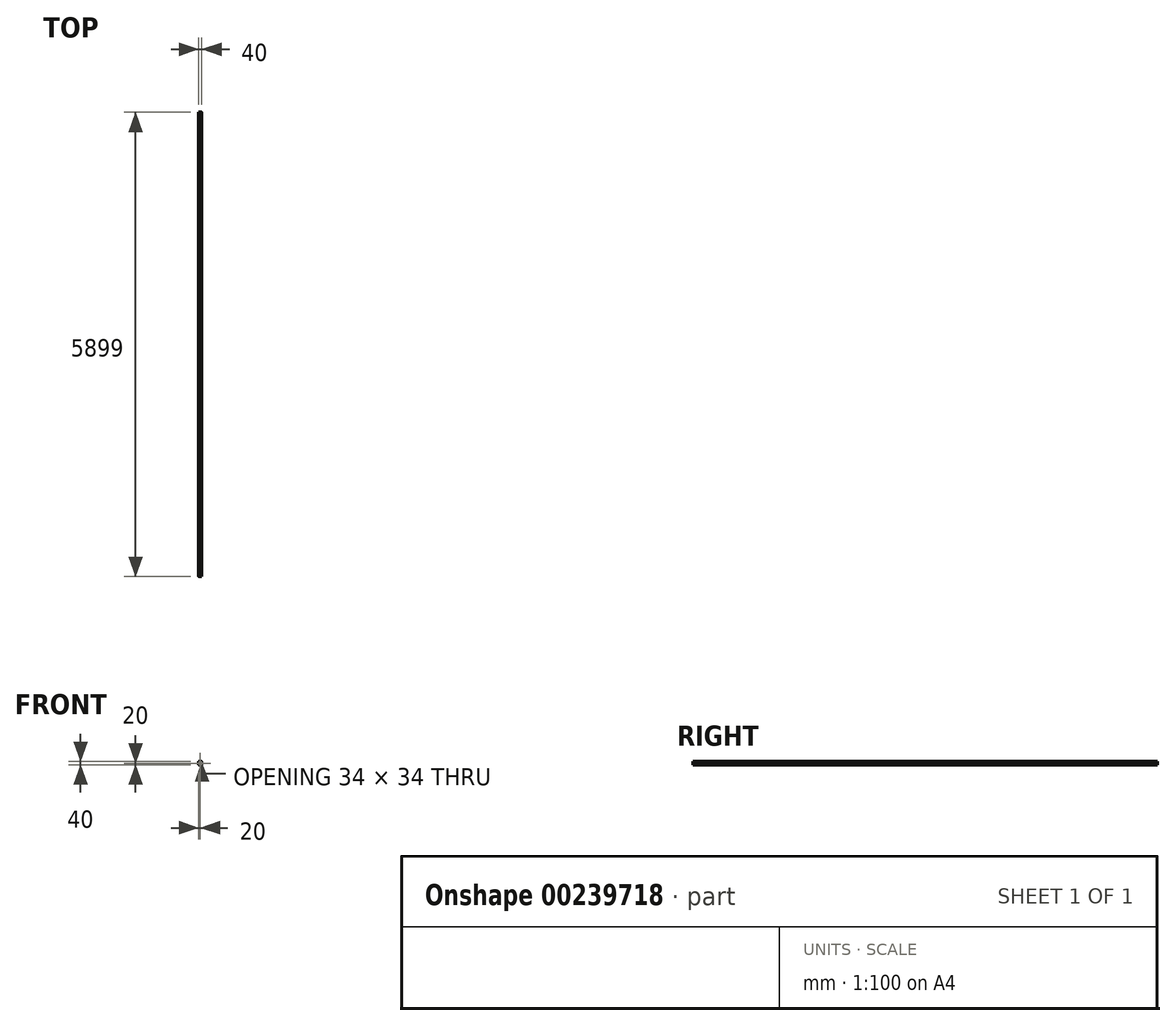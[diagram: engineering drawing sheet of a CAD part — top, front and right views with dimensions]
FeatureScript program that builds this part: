
annotation { "Feature Type Name" : "Feature", "Feature Type Description" : "" }
export const myFeature = defineFeature(function(context is Context, id is Id, definition is map)
    precondition{}
    {
        {
            var Q0;
            Q0=qCreatedBy(makeId("Front.planeOp"),FACE);
            var sketch = newSketch(context, id + "F0", { "sketchPlane" : qUnion([Q0])});
            skLineSegment(sketch, "E0.bottom", {"start": v(16, 20) * mm, "end": v(-16, 20) * mm});
            skLineSegment(sketch, "E0.top", {"start": v(16, -20) * mm, "end": v(-16, -20) * mm});
            skLineSegment(sketch, "E0.left", {"start": v(20, 16) * mm, "end": v(20, -16) * mm});
            skLineSegment(sketch, "E0.right", {"start": v(-20, 16) * mm, "end": v(-20, -16) * mm});
            skPoint(sketch, "E0.middle", {"position": v(0, 0) * mm});
            skPoint(sketch, "E1.visualSharp", {"position": v(-20, 20) * mm});
            skArc(sketch, "E1.filletArc", {"start": v(-16, 20) * mm, "mid": v(-18.83, 18.83) * mm, "end": v(-20, 16) * mm});
            skPoint(sketch, "E2.visualSharp", {"position": v(20, 20) * mm});
            skArc(sketch, "E2.filletArc", {"start": v(20, 16) * mm, "mid": v(18.83, 18.83) * mm, "end": v(16, 20) * mm});
            skPoint(sketch, "E3.visualSharp", {"position": v(20, -20) * mm});
            skArc(sketch, "E3.filletArc", {"start": v(16, -20) * mm, "mid": v(18.83, -18.83) * mm, "end": v(20, -16) * mm});
            skPoint(sketch, "E4.visualSharp", {"position": v(-20, -20) * mm});
            skArc(sketch, "E4.filletArc", {"start": v(-20, -16) * mm, "mid": v(-18.83, -18.83) * mm, "end": v(-16, -20) * mm});
            skLineSegment(sketch, "E5.0", {"start": v(16, 17) * mm, "end": v(-16, 17) * mm});
            skArc(sketch, "E5.1", {"start": v(17, 16) * mm, "mid": v(16.7, 16.7) * mm, "end": v(16, 17) * mm});
            skArc(sketch, "E5.2", {"start": v(-16, 17) * mm, "mid": v(-16.7, 16.7) * mm, "end": v(-17, 16) * mm});
            skLineSegment(sketch, "E5.3", {"start": v(17, 16) * mm, "end": v(17, -16) * mm});
            skLineSegment(sketch, "E5.4", {"start": v(-17, 16) * mm, "end": v(-17, -16) * mm});
            skArc(sketch, "E5.5", {"start": v(-17, -16) * mm, "mid": v(-16.7, -16.7) * mm, "end": v(-16, -17) * mm});
            skLineSegment(sketch, "E5.6", {"start": v(16, -17) * mm, "end": v(-16, -17) * mm});
            skArc(sketch, "E5.7", {"start": v(16, -17) * mm, "mid": v(16.7, -16.7) * mm, "end": v(17, -16) * mm});
            skSolve(sketch);
        }
        {
            var Q0;
            Q0=makeQuery(id+"F0.imprint","IMPRINT",FACE,{"disambiguationData":[TD([[makeQuery(id+"F0.imprint","IMPRINT",EDGE,{"derivedFrom":sQuery(id+"F0.wireOp",EDGE,"E0.bottom")}),1.0]])]});
            extrude(context, id + "F1", {"entities" : qUnion([Q0]), "depth" : 5899 * mm});
        }
    });
